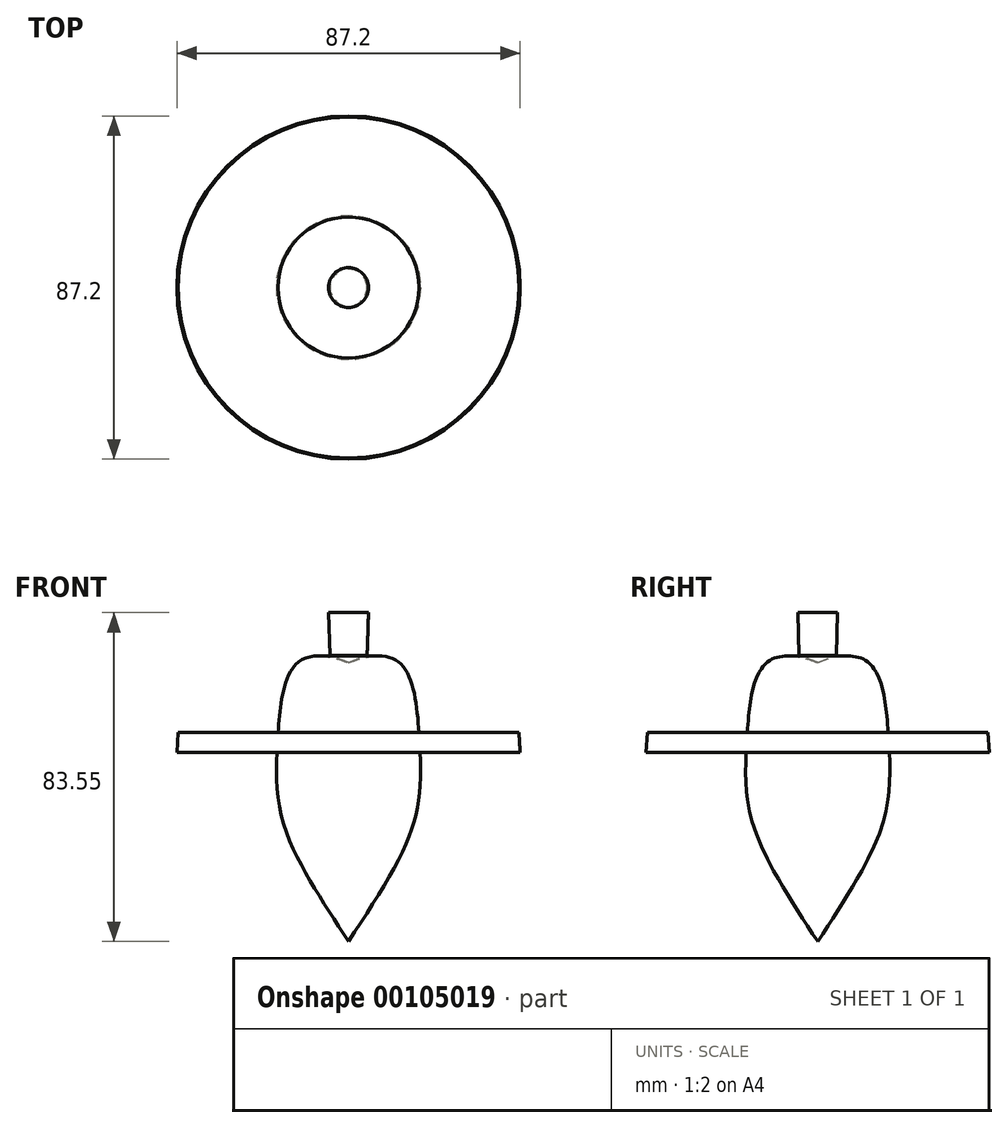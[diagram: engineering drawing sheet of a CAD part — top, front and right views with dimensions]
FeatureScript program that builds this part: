
annotation { "Feature Type Name" : "Feature", "Feature Type Description" : "" }
export const myFeature = defineFeature(function(context is Context, id is Id, definition is map)
    precondition{}
    {
        {
            var Q0;
            Q0=qCreatedBy(makeId("Front.planeOp"),FACE);
            var sketch = newSketch(context, id + "F0", { "sketchPlane" : qUnion([Q0])});
            skLineSegment(sketch, "E0", {"start": v(0, 0) * mm, "end": v(0, 34.4) * mm});
            skLineSegment(sketch, "E1", {"start": v(0, 34.4) * mm, "end": v(0, -36.44) * mm});
            skFitSpline(sketch, "E2", {"points": [v(0, 34.4) * mm, v(12.95, 34.4) * mm, v(17.9, 16.65) * mm, v(17.9, 0) * mm, v(13.62, -13.77) * mm, v(0, -36.44) * mm], "startDerivative": vector(82.42, 33) * mm, "endDerivative": vector(-63.55, -97.56) * mm});
            skLineSegment(sketch, "E3", {"start": v(17.9, 16.65) * mm, "end": v(43.3, 16.65) * mm});
            skLineSegment(sketch, "E4", {"start": v(43.3, 16.65) * mm, "end": v(43.6, 11.58) * mm});
            skLineSegment(sketch, "E5", {"start": v(43.6, 11.58) * mm, "end": v(18.2, 11.58) * mm});
            skLineSegment(sketch, "E6", {"start": v(0, 34.4) * mm, "end": v(0, 47.1) * mm});
            skLineSegment(sketch, "E7", {"start": v(0, 47.1) * mm, "end": v(5.08, 47.1) * mm});
            skLineSegment(sketch, "E8", {"start": v(5.08, 47.1) * mm, "end": v(4.73, 36.3) * mm});
            skLineSegment(sketch, "E9", {"start": v(4.73, 36.3) * mm, "end": v(0, 34.4) * mm});
            skSolve(sketch);
        }
        {
            var Q0;
            {var subQ0=sQuery(id+"F0.wireOp",EDGE,"E3");Q0=makeQuery(id+"F0.imprint","IMPRINT",FACE,{"disambiguationData":[TD([[makeQuery(id+"F0.imprint","IMPRINT",EDGE,{"derivedFrom":subQ0}),-1.0]])]});}
            var Q1;
            {var subQ0=sQuery(id+"F0.wireOp",EDGE,"E2");var subQ4=makeQuery(id+"F0.imprint","INTERSECT",VERTEX,{"derivedFrom":[subQ0,sQuery(id+"F0.wireOp",EDGE,"E3")]});Q1=makeQuery(id+"F0.imprint","IMPRINT",FACE,{"disambiguationData":[TD([[makeQuery(id+"F0.imprint","IMPRINT",EDGE,{"disambiguationData":[TD([[subQ4,-1.0]])],"derivedFrom":subQ0}),-1.0]])]});}
            var Q2;
            Q2=makeQuery(id+"F0.imprint","IMPRINT",FACE,{"disambiguationData":[TD([[makeQuery(id+"F0.imprint","IMPRINT",EDGE,{"derivedFrom":sQuery(id+"F0.wireOp",EDGE,"E6")}),-1.0]])]});
            var Q3;
            Q3=sQuery(id+"F0.wireOp",EDGE,"E1");
            revolve(context, id + "F1", {"entities" : qUnion([Q0, Q1, Q2]), "axis" : qUnion([Q3]), "revolveType" : RevolveType.FULL});
        }
    });
